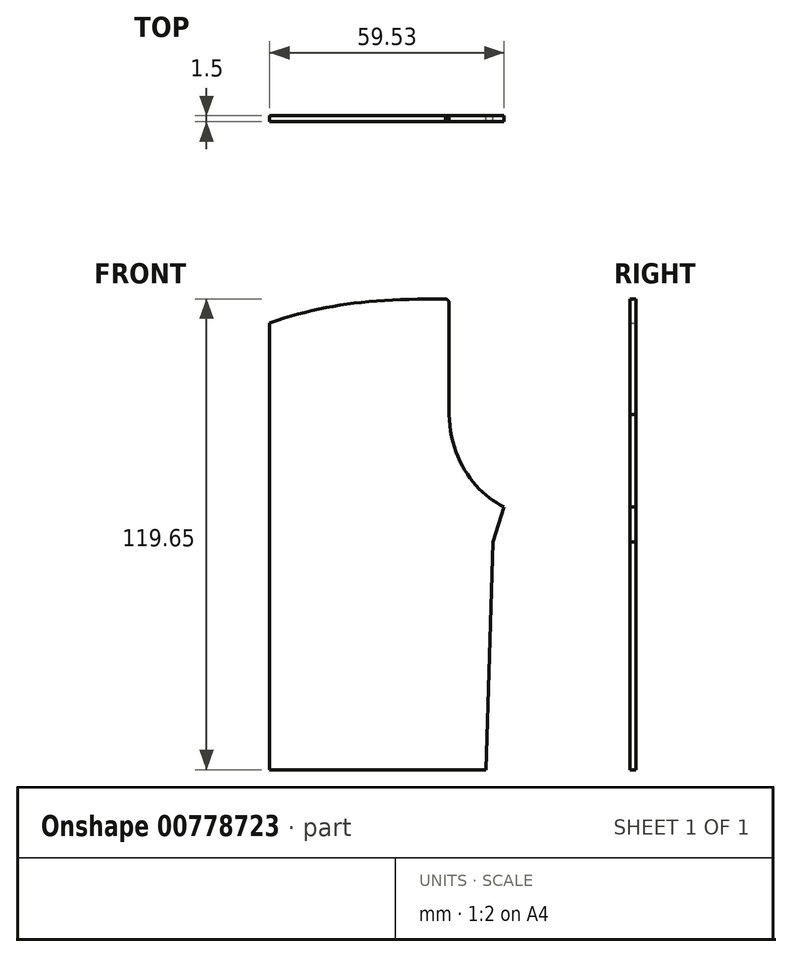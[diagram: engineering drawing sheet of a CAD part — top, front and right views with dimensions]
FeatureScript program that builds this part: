
annotation { "Feature Type Name" : "Feature", "Feature Type Description" : "" }
export const myFeature = defineFeature(function(context is Context, id is Id, definition is map)
    precondition{}
    {
        {
            var Q0;
            Q0=qCreatedBy(makeId("Front.planeOp"),FACE);
            var sketch = newSketch(context, id + "F0", { "sketchPlane" : qUnion([Q0])});
            skLineSegment(sketch, "E0", {"start": v(0, 0) * mm, "end": v(55, 0) * mm});
            skLineSegment(sketch, "E1", {"start": v(55, 0) * mm, "end": v(56.79, 57.84) * mm});
            skLineSegment(sketch, "E2", {"start": v(56.79, 57.84) * mm, "end": v(59.53, 66.82) * mm});
            skLineSegment(sketch, "E3", {"start": v(0, 0) * mm, "end": v(0, 113.54) * mm});
            skFitSpline(sketch, "E4", {"points": [v(0, 113.54) * mm, v(44.65, 119.65) * mm], "startDerivative": vector(42.5, 14.54) * mm, "endDerivative": vector(56.66, 0) * mm});
            skFitSpline(sketch, "E5", {"points": [v(44.65, 119.65) * mm, v(45.62, 118.32) * mm], "startDerivative": vector(1.89, -0.48) * mm, "endDerivative": vector(0, -2.29) * mm});
            skLineSegment(sketch, "E6", {"start": v(45.62, 118.32) * mm, "end": v(45.62, 90.3) * mm});
            skFitSpline(sketch, "E7", {"points": [v(45.62, 90.3) * mm, v(59.53, 66.82) * mm], "startDerivative": vector(0.44, -34.03) * mm, "endDerivative": vector(22, -10.48) * mm});
            skLineSegment(sketch, "E8", {"start": v(44.65, 119.65) * mm, "end": v(0, 119.65) * mm, "construction": true});
            skLineSegment(sketch, "E9", {"start": v(0, 119.65) * mm, "end": v(0, 113.54) * mm, "construction": true});
            skLineSegment(sketch, "E10", {"start": v(59.53, 66.82) * mm, "end": v(59.53, 0) * mm, "construction": true});
            skLineSegment(sketch, "E11", {"start": v(59.53, 0) * mm, "end": v(55, 0) * mm, "construction": true});
            skSolve(sketch);
        }
        {
            var Q0;
            Q0=qSketchRegion(id+"F0",true);
            extrude(context, id + "F1", {"entities" : qUnion([Q0]), "depth" : 1.5 * mm, "offsetDistance" : 25 * mm});
        }
    });
